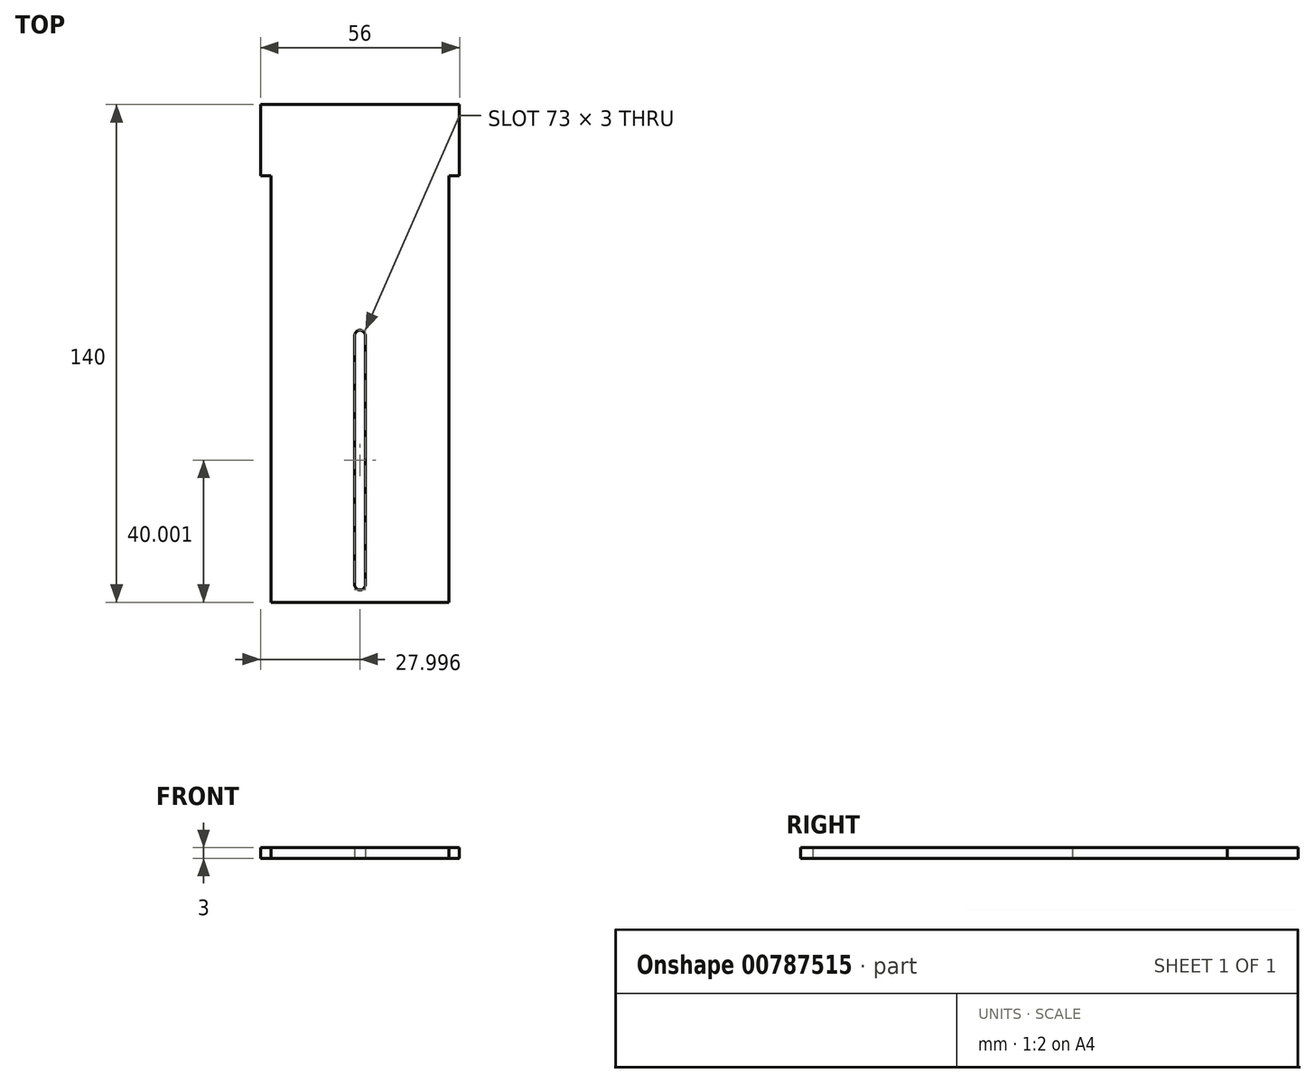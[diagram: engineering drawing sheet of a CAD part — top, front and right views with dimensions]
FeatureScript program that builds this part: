
annotation { "Feature Type Name" : "Feature", "Feature Type Description" : "" }
export const myFeature = defineFeature(function(context is Context, id is Id, definition is map)
    precondition{}
    {
        {
            var Q0;
            Q0=qCreatedBy(makeId("Top.planeOp"),FACE);
            var sketch = newSketch(context, id + "F0", { "sketchPlane" : qUnion([Q0])});
            skLineSegment(sketch, "E0.bottom", {"start": v(-92.6, -120.5) * mm, "end": v(-42.6, -120.5) * mm});
            skLineSegment(sketch, "E0.top", {"start": v(-92.6, 19.5) * mm, "end": v(-42.6, 19.5) * mm});
            skLineSegment(sketch, "E0.left", {"start": v(-92.6, -120.5) * mm, "end": v(-92.6, -0.5) * mm});
            skLineSegment(sketch, "E0.right", {"start": v(-42.6, -120.5) * mm, "end": v(-42.6, -0.5) * mm});
            skLineSegment(sketch, "E1.bottom", {"start": v(-92.6, 19.5) * mm, "end": v(-95.6, 19.5) * mm});
            skLineSegment(sketch, "E1.top", {"start": v(-92.6, -0.5) * mm, "end": v(-95.6, -0.5) * mm});
            skLineSegment(sketch, "E1.right", {"start": v(-95.6, 19.5) * mm, "end": v(-95.6, -0.5) * mm});
            skLineSegment(sketch, "E2.bottom", {"start": v(-42.6, 19.5) * mm, "end": v(-39.6, 19.5) * mm});
            skLineSegment(sketch, "E2.top", {"start": v(-42.6, -0.5) * mm, "end": v(-39.6, -0.5) * mm});
            skLineSegment(sketch, "E2.right", {"start": v(-39.6, 19.5) * mm, "end": v(-39.6, -0.5) * mm});
            skLineSegment(sketch, "E3", {"start": v(-67.6, -120.5) * mm, "end": v(-67.6, 19.5) * mm, "construction": true});
            skLineSegment(sketch, "E4.left", {"start": v(-69.1, -45.5) * mm, "end": v(-69.1, -115.5) * mm});
            skLineSegment(sketch, "E4.right", {"start": v(-66.1, -45.5) * mm, "end": v(-66.1, -115.5) * mm});
            skPoint(sketch, "E4.middle", {"position": v(-67.6, -80.5) * mm});
            skArc(sketch, "E5", {"start": v(-66.1, -45.5) * mm, "mid": v(-67.6, -44) * mm, "end": v(-69.1, -45.5) * mm});
            skArc(sketch, "E6", {"start": v(-69.1, -115.5) * mm, "mid": v(-67.6, -117) * mm, "end": v(-66.1, -115.5) * mm});
            skSolve(sketch);
        }
        {
            var Q0;
            Q0=makeQuery(id+"F0.imprint","IMPRINT",FACE,{"disambiguationData":[TD([[makeQuery(id+"F0.imprint","IMPRINT",EDGE,{"derivedFrom":sQuery(id+"F0.wireOp",EDGE,"E0.bottom")}),1.0]])]});
            extrude(context, id + "F1", {"entities" : qUnion([Q0]), "depth" : 3 * mm, "offsetDistance" : 25.4 * mm});
        }
    });
